# Revit family: GP Radiator Control Valve Straight Model 5523
name_source: partatom
category: Rohrzubehör
units: mm (PartAtom-declared; Revit-internal decimal feet)

## family parameters
Arbeitsebenenbasiert = Nein
Beim Laden mit Abzugskörper schneiden = Nein
Bemaßung runder Anschluss = Durchmesser verwenden
Gemeinsam genutzt = Nein
Immer vertikal = Ja
OmniClass-Nummer = 23.65.55.14
OmniClass-Titel = Valves for Liquid Services
Teiletyp = Unterbricht

## types (1)
- GP Radiator Control Valve Straight Model 5523
    Body = nickel-plated
    H01 = 17 mm
    H02 = 25.5 mm
    Hand wheel = plastic, white
    Hersteller = HERZ Armaturen Ges.m.b.H.
    LO1 = 10.5 mm  [stored 0.0344488 ft]
    Max. operating pressure = 1000000.0 Pa
    Max. operating temperature = 110 °C
    Medium = Hot water quality according to Austrian standard ÖNORM H 5195 and/or VDI guideline 2035.
    Model = These universal models are nickel-plated and equipped with special sockets for threaded pipe and compression union connections.
    R01 = 10.5 mm  [stored 0.0344488 ft]
    R02 = 11.5 mm  [stored 0.0377297 ft]
    R03 = 28 mm
    R04 = 2 mm  [stored 0.00656168 ft]
    R05 = 25 mm  [stored 0.082021 ft]
    S01 = 10 mm  [stored 0.0328084 ft]
    S03 = 61 mm  [stored 0.200131 ft]
    S04 = 45 mm  [stored 0.147638 ft]
    SCRNCODE = 05;00;02
    SCRNSEQ = ARM;ARM_TYP="ALLF";2
    URL = www.herzvalves.com
    Vorgabe-Ansicht = 0 mm  [stored 0 ft]
    W01 = 60.00°

note: [stored X ft] marks values corroborated as IEEE doubles in the binary element streams (Revit-internal decimal feet)
